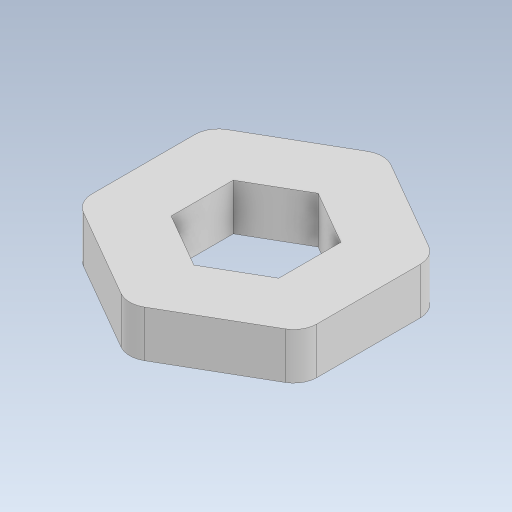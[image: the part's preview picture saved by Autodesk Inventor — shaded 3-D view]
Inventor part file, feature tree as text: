
AUTODESK INVENTOR PART (.ipt)
format: ipt  version: 2023 (Build 270158000, 158)  size: 111,616 bytes
history: native  units: in
note: dims shown in document units (in); Inventor stores cm internally (conversion verified against a paired STEP export)
features: extrude x1, fillet x1, sketch x1
ambient origin geometry x8: Origin, YZ Plane, XZ Plane, XY Plane, X Axis, Y Axis, Z Axis, Center Point
bodies: Solid1 (feature_tree)
feature tree (3):
  extrude  "Extrusion1"  Depth=0.7in
  fillet  "Fillet1"  Radius=0.25in
  sketch  "Sketch1"  dims[d0=0.3346in d1=0.7in d2=0.25in d3=0.0in d4=0.125in]
